# Revit family: Crealco Evolution H
name_source: partatom
category: Windows
revit_build: Autodesk Revit 2016 (Build: 20150714_1515(x64)
units: mm (PartAtom-declared; Revit-internal decimal feet)

## family parameters
Always vertical = Yes
Cut with Voids When Loaded = No
Host = Wall
OmniClass Number = 23.30.20.00
OmniClass Title = Windows
Room Calculation Point = No
Shared = No

## types (5) — shared parameters
54mm Mullion Inertia = 12.55
75mm Mullion = No
75mm Mullion Inertia = 31
Default Sill Height = 800 mm  [stored 2.62467 ft]
Description = Bottom Hung Open In Window
Fixed Panel Top Gap = 27 mm  [stored 0.0885827 ft]
Limit Fixed Panel Height Max = 6000 mm  [stored 19.685 ft]
Limit Fixed Panel Height Min = 100 mm  [stored 0.328084 ft]
Limit Glazing Thickness Max = 6 mm  [stored 0.019685 ft]
Limit Glazing Thickness Min = 4 mm  [stored 0.0131234 ft]
Limit Mullion 1 Spacing Min = 230 mm  [stored 0.754593 ft]
Limit Sash Height Max = 700 mm  [stored 2.29659 ft]
Limit Sash Height Min = 200 mm  [stored 0.656168 ft]
Limit Sash Width Max = 850 mm  [stored 2.78871 ft]
Limit Sash Width Min = 200 mm  [stored 0.656168 ft]
Limit Window Height Max = 7495 mm
Limit Window Height Min = 595 mm  [stored 1.9521 ft]
Limit Window Width Max = 1760 mm
Limit Window Width Min = 460 mm  [stored 1.50919 ft]
Manufacturer = Crealco
Max Wind Load = 10000
Model = Evolution
Mullion Width = 20 mm  [stored 0.0656168 ft]
Sash Mullion Gap = 10 mm  [stored 0.0328084 ft]
Sash Offset = 5 mm  [stored 0.0164042 ft]
Sash Side Gap = 20 mm  [stored 0.0656168 ft]
Sash Transom Gap = 10 mm  [stored 0.0328084 ft]
Standard Mullion Inertia = 2.36
Standard Transom 2 Top Gap = 593 mm  [stored 1.94554 ft]
Transom Fixed Panel Gap = 18 mm
Transom Mullion Side Gap = 18 mm
Transom Side Gap = 27 mm  [stored 0.0885827 ft]
URL = https://www.crealco.co.za
Wall Closure = By host
zero-valued in all types: Min Wind Load

## per-type parameters (varying)
| type | Standard Height | Standard Size | Standard Transom 1 Top Gap | Standard Width | Type Comments |
| 1190 x 1490mm (EVOL-1215DB) | 1490 mm  [stored 4.88845 ft] | Yes | 295 mm  [stored 0.967848 ft] | 1190 mm  [stored 3.9042 ft] | EVOL-1215DB |
| User Defined | 1490 mm  [stored 4.88845 ft] | No | 295 mm  [stored 0.967848 ft] | 1190 mm  [stored 3.9042 ft] | Custom |
| 1761 x 1490mm (EVOL-1815DB) | 1490 mm  [stored 4.88845 ft] | Yes | 295 mm  [stored 0.967848 ft] | 1761 mm  [stored 5.77756 ft] | EVOL-1815DB |
| 1190 x 1790mm (EVOL-1218DB) | 1790 mm  [stored 5.8727 ft] | Yes | 595 mm  [stored 1.9521 ft] | 1190 mm  [stored 3.9042 ft] | EVOL-1218DB |
| 1761 x 1790mm (EVOL-1818DB) | 1790 mm  [stored 5.8727 ft] | Yes | 595 mm  [stored 1.9521 ft] | 1761 mm  [stored 5.77756 ft] | EVOL-1818DB |

note: [stored X ft] marks values corroborated as IEEE doubles in the binary element streams (Revit-internal decimal feet)

## geometry (parser evidence)
native form markers: Sweep x15
no freeform markers — native parametric forms only
